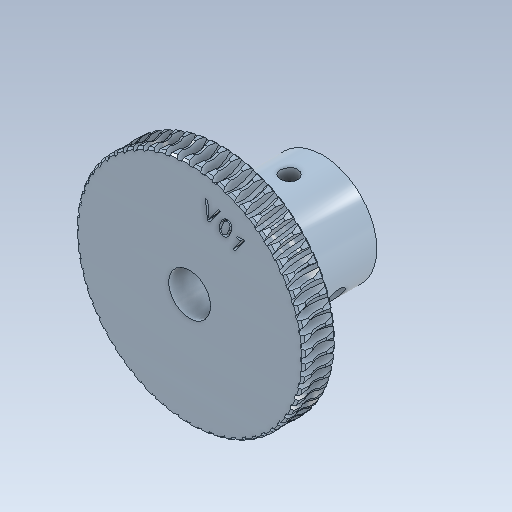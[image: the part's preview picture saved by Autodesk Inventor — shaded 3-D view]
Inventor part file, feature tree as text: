
AUTODESK INVENTOR PART (.ipt)
format: ipt  version: 2021.1 (Build 251245010, 245A)  size: 1,276,416 bytes
history: native  units: mm (DEFAULTED — no unit token found)
features: other x8, plane x4, sketch x4, extrude x3, pattern_circular x2, hole x1
ambient origin geometry x5: Origin, X Axis, Y Axis, Z Axis, Center Point
bodies: Solid1 (feature_tree)
feature tree (22):
  other  "Tooth Plane"
  other  "Base Body Sketch"
  other  "Base Body"
  other  "Base Body2"
  plane  "Work Plane13"
  other  "Tooth"
  pattern_circular  "Tooth Pattern"  [2 undecoded]
  plane  "Work Plane14"
  plane  "Work Plane15"
  extrude  "Extrusion1"  Depth=6.87231mm
  extrude  "Extrusion3"  Depth=1.2954mm
  plane  "Work Plane16"
  hole  "Hole3"  [1 undecoded]
  pattern_circular  "Circular Pattern2"  Count=60  [1 undecoded]
  extrude  "Extrusion4"  TaperAngle=360.0deg  [1 undecoded]
  other  "Tooth Sketch"
  sketch  "Sketch8"  dims[d35=90.0deg]
  other  "Srf1"
  sketch  "Sketch9"  dims[d37=-0.996687mm]
  sketch  "Sketch11"  dims[d38=48.106173mm]
  sketch  "Sketch13"  dims[d39=3.490659mm d40=5.222956mm d41=6.87231mm d42=1.2954mm d43=90.0deg d44=600.0mm d46=360.0deg d50=8.416543mm d68=48.106173mm d69=0.0mm d73=0.0mm d75=0.523599mm d77=82.467725mm d78=12.3mm d79=0.0mm d80=0.0mm d81=0.0mm d82=0.0mm d83=0.523599mm d84=0.0mm d85=180.0deg d86=48.106173mm d87=86.591112mm d89=10.995697mm d90=90.0deg d92=12.3mm d93=48.106173mm d94=15.875mm d95=0.0mm d96=0.0mm d100=41.275mm d101=38.1mm d102=0.0mm d103=5.1054mm d104=19.05mm d105=6.5278mm d106=9.525mm d107=14.3117mm d108=15.24mm d109=20.594885mm d110=30.0mm d111=360.0deg d113=63.5mm d114=2.54mm d115=0.0mm d116=25.4mm]
  other  "Pitch Diameter"
note: 5 required parameter values undecoded (feature->parameter linkage not recoverable at this tier; creation-order binding heuristic only, values carry confidence <= 0.55)
